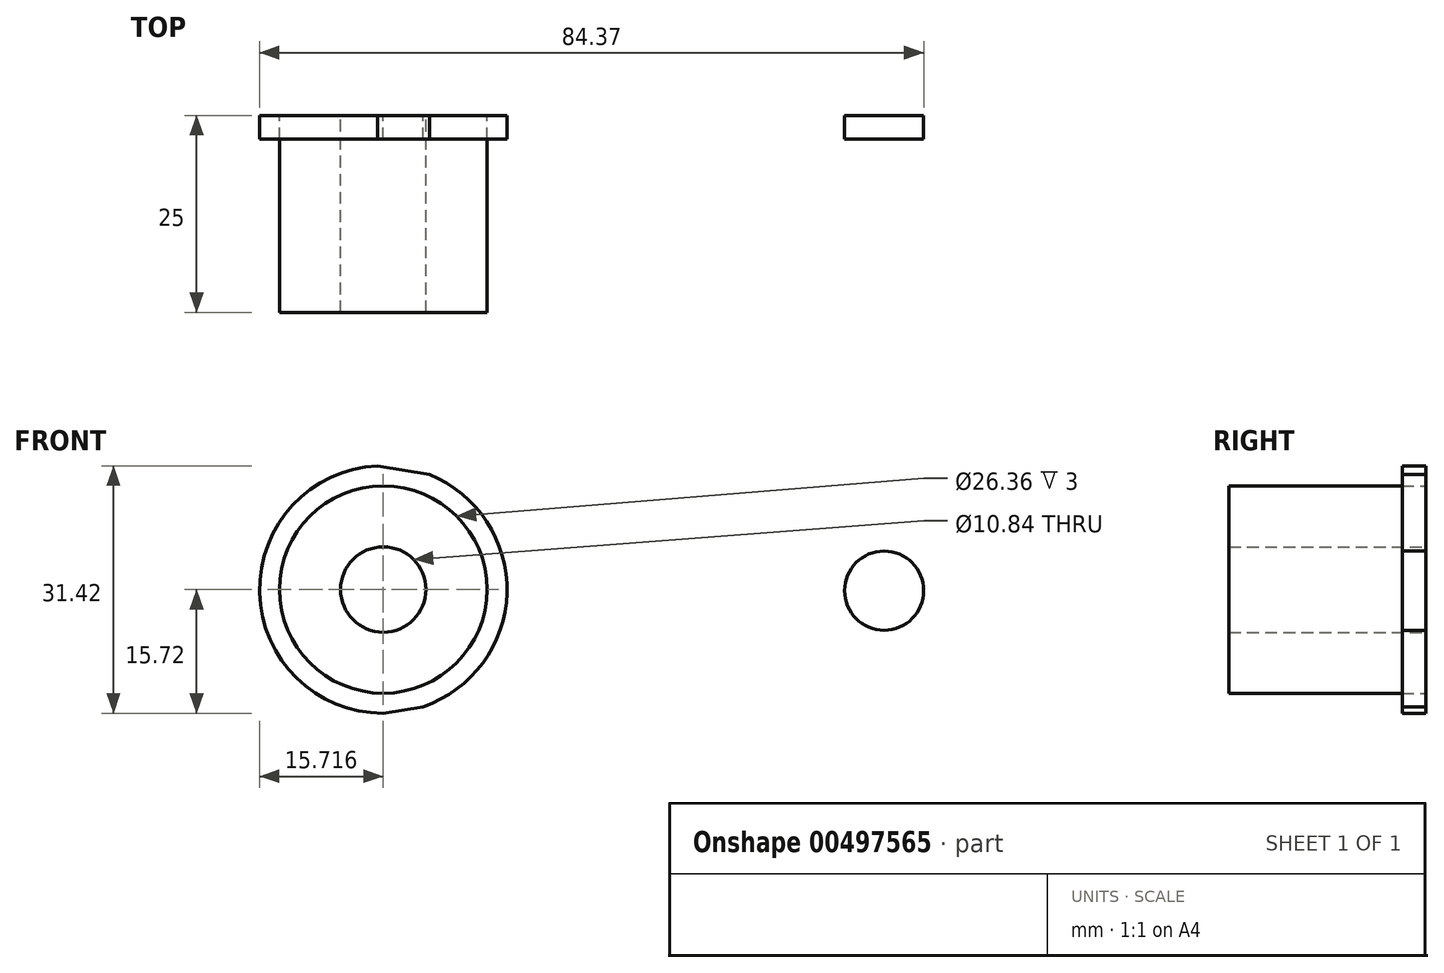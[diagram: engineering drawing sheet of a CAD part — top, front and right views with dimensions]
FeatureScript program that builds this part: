
annotation { "Feature Type Name" : "Feature", "Feature Type Description" : "" }
export const myFeature = defineFeature(function(context is Context, id is Id, definition is map)
    precondition{}
    {
        {
            var Q0;
            Q0=qCreatedBy(makeId("Front.planeOp"),FACE);
            var sketch = newSketch(context, id + "F0", { "sketchPlane" : qUnion([Q0])});
            skCircle(sketch, "E0", {"center": v(-42.51, 0) * mm, "radius": 15.72 * mm});
            skCircle(sketch, "E1", {"center": v(21.1, -0.15) * mm, "radius": 5.03 * mm});
            skCircle(sketch, "E2", {"center": v(-42.51, 0) * mm, "radius": 13.18 * mm});
            skLineSegment(sketch, "E3", {"start": v(-42.51, -15.72) * mm, "end": v(21.26, -5.17) * mm});
            skLineSegment(sketch, "E4", {"start": v(-43.25, 15.7) * mm, "end": v(20.81, 4.87) * mm});
            skCircle(sketch, "E5", {"center": v(-42.51, 0) * mm, "radius": 5.42 * mm});
            skSolve(sketch);
        }
        {
            var Q0;
            Q0=makeQuery(id+"F0.imprint","IMPRINT",FACE,{"disambiguationData":[TD([[makeQuery(id+"F0.imprint","IMPRINT",EDGE,{"derivedFrom":sQuery(id+"F0.wireOp",EDGE,"E2")}),1.0]])]});
            extrude(context, id + "F1", {"entities" : qUnion([Q0]), "depth" : 25 * mm});
        }
        {
            var Q0;
            {var subQ0=sQuery(id+"F0.wireOp",EDGE,"E4");var subQ1=sQuery(id+"F0.wireOp",EDGE,"E0");var subQ2=makeQuery(id+"F0.imprint","INTERSECT",VERTEX,{"disambiguationData":[OD(1.0)],"derivedFrom":[subQ1,subQ0]});Q0=makeQuery(id+"F0.imprint","IMPRINT",FACE,{"disambiguationData":[TD([[makeQuery(id+"F0.imprint","IMPRINT",EDGE,{"disambiguationData":[TD([[subQ2,1.0]])],"derivedFrom":subQ1}),-1.0]])]});}
            var Q1;
            {var subQ0=sQuery(id+"F0.wireOp",EDGE,"E3");var subQ1=sQuery(id+"F0.wireOp",EDGE,"E0");var subQ2=makeQuery(id+"F0.imprint","INTERSECT",VERTEX,{"disambiguationData":[OD(0.0)],"derivedFrom":[subQ1,subQ0]});Q1=makeQuery(id+"F0.imprint","IMPRINT",FACE,{"disambiguationData":[TD([[makeQuery(id+"F0.imprint","IMPRINT",EDGE,{"disambiguationData":[TD([[subQ2,-1.0]])],"derivedFrom":subQ1}),1.0]])]});}
            var Q2;
            {var subQ0=sQuery(id+"F0.wireOp",EDGE,"E1");var subQ1=makeQuery(id+"F0.imprint","INTERSECT",VERTEX,{"derivedFrom":[subQ0,sQuery(id+"F0.wireOp",EDGE,"E3")]});Q2=makeQuery(id+"F0.imprint","IMPRINT",FACE,{"disambiguationData":[TD([[makeQuery(id+"F0.imprint","IMPRINT",EDGE,{"disambiguationData":[TD([[subQ1,1.0]])],"derivedFrom":subQ0}),1.0]])]});}
            var Q3;
            {var subQ0=sQuery(id+"F0.wireOp",EDGE,"E4");var subQ1=sQuery(id+"F0.wireOp",EDGE,"E0");var subQ2=makeQuery(id+"F0.imprint","INTERSECT",VERTEX,{"disambiguationData":[OD(0.0)],"derivedFrom":[subQ1,subQ0]});Q3=makeQuery(id+"F0.imprint","IMPRINT",FACE,{"disambiguationData":[TD([[makeQuery(id+"F0.imprint","IMPRINT",EDGE,{"disambiguationData":[TD([[subQ2,1.0]])],"derivedFrom":subQ1}),1.0]])]});}
            var Q4;
            {var subQ0=sQuery(id+"F0.wireOp",EDGE,"E4");var subQ1=sQuery(id+"F0.wireOp",EDGE,"E0");var subQ2=makeQuery(id+"F0.imprint","INTERSECT",VERTEX,{"disambiguationData":[OD(1.0)],"derivedFrom":[subQ1,subQ0]});Q4=makeQuery(id+"F0.imprint","IMPRINT",FACE,{"disambiguationData":[TD([[makeQuery(id+"F0.imprint","IMPRINT",EDGE,{"disambiguationData":[TD([[subQ2,1.0]])],"derivedFrom":subQ1}),-1.0]])]});}
            var Q5;
            Q5=makeQuery(id+"F0.imprint","IMPRINT",FACE,{"disambiguationData":[TD([[makeQuery(id+"F0.imprint","IMPRINT",EDGE,{"derivedFrom":sQuery(id+"F0.wireOp",EDGE,"E2")}),-1.0]])]});
            extrude(context, id + "F2", {"entities" : qUnion([Q0, Q1, Q2, Q3, Q4, Q5]), "depth" : 3 * mm});
        }
        {
            var Q0;
            Q0=sQuery(id+"F0.wireOp",EDGE,"E1");
            extrude(context, id + "F3", {"bodyType" : ToolBodyType.SURFACE, "surfaceEntities" : qUnion([Q0]), "depth" : 4 * mm});
        }
        {
            var Q0;
            Q0=sQuery(id+"F0.wireOp",EDGE,"E0");
            var Q1;
            Q1=sQuery(id+"F0.wireOp",EDGE,"E2");
            extrude(context, id + "F4", {"bodyType" : ToolBodyType.SURFACE, "surfaceEntities" : qUnion([Q0, Q1]), "depth" : 10 * mm});
        }
    });
